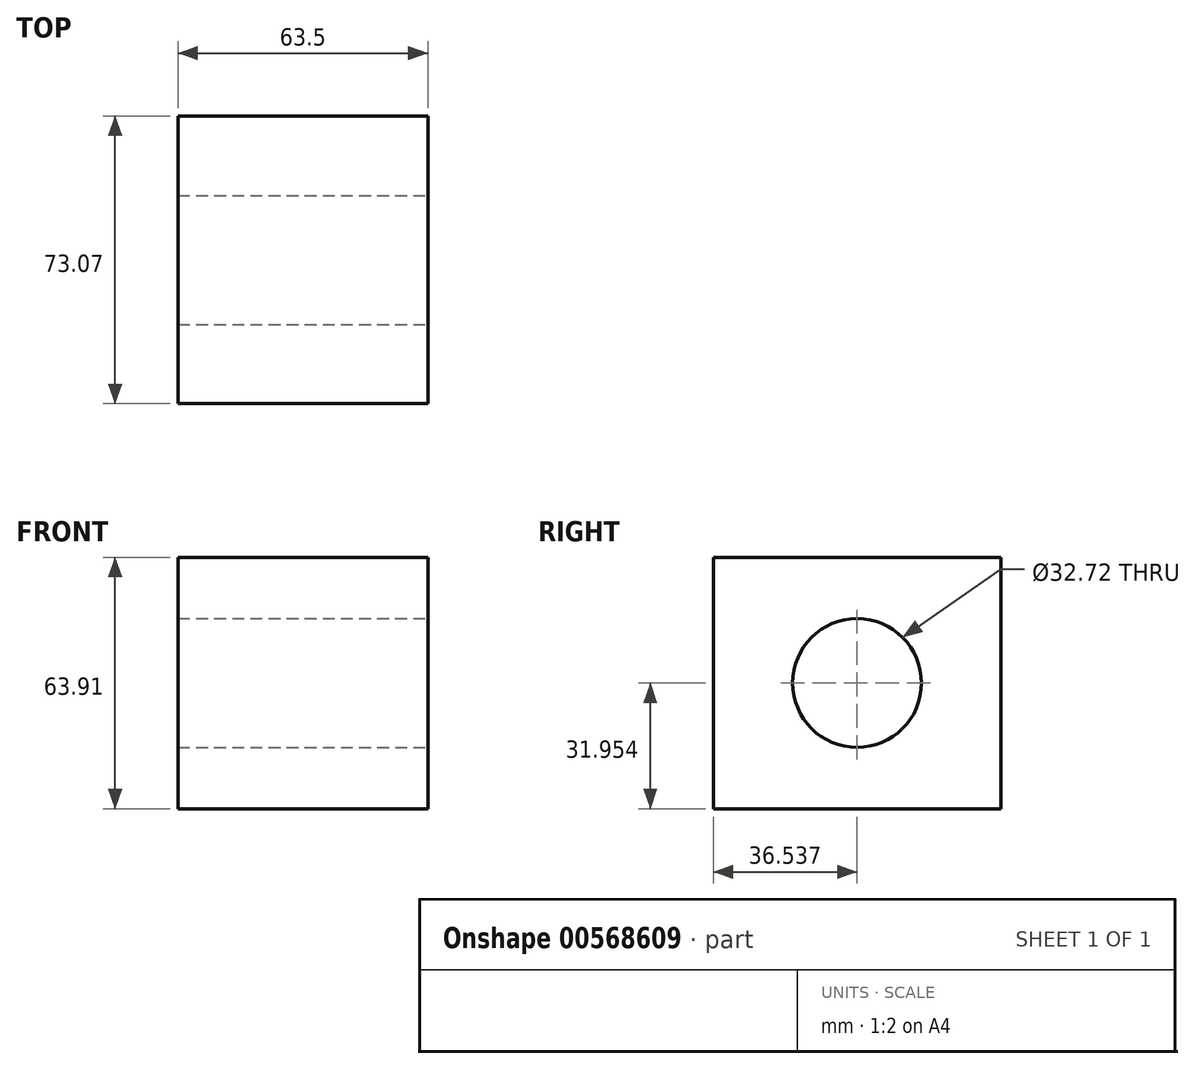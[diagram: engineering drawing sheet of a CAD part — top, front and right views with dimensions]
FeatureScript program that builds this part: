
annotation { "Feature Type Name" : "Feature", "Feature Type Description" : "" }
export const myFeature = defineFeature(function(context is Context, id is Id, definition is map)
    precondition{}
    {
        {
            var Q0;
            Q0=qCreatedBy(makeId("Right.planeOp"),FACE);
            var sketch = newSketch(context, id + "F0", { "sketchPlane" : qUnion([Q0])});
            skLineSegment(sketch, "E0.bottom", {"start": v(0, 0) * mm, "end": v(73.07, 0) * mm});
            skLineSegment(sketch, "E0.top", {"start": v(0, 63.9) * mm, "end": v(73.07, 63.9) * mm});
            skLineSegment(sketch, "E0.left", {"start": v(0, 0) * mm, "end": v(0, 63.9) * mm});
            skLineSegment(sketch, "E0.right", {"start": v(73.07, 0) * mm, "end": v(73.07, 63.9) * mm});
            skSolve(sketch);
        }
        {
            var Q0;
            Q0=makeQuery(id+"F0.imprint","IMPRINT",FACE,{"disambiguationData":[TD([[makeQuery(id+"F0.imprint","IMPRINT",EDGE,{"derivedFrom":sQuery(id+"F0.wireOp",EDGE,"E0.bottom")}),1.0]])]});
            extrude(context, id + "F1", {"entities" : qUnion([Q0]), "depth" : 63.5 * mm, "offsetDistance" : 25.4 * mm});
        }
        {
            var Q0;
            Q0=makeQuery(id+"F1.opExtrude","CAP_FACE",FACE,{"disambiguationData":[OSD([sQuery(id+"F0.wireOp",EDGE,"E0.bottom"),sQuery(id+"F0.wireOp",EDGE,"E0.top"),sQuery(id+"F0.wireOp",EDGE,"E0.left"),sQuery(id+"F0.wireOp",EDGE,"E0.right")])],"isStart":false});
            var sketch = newSketch(context, id + "F2", { "sketchPlane" : qUnion([Q0])});
            skArc(sketch, "E1", {"start": v(33.92, 15.8) * mm, "mid": v(30.07, 19.46) * mm, "end": v(24.87, 20.49) * mm});
            skCircle(sketch, "E2", {"center": v(36.54, 31.95) * mm, "radius": 16.36 * mm});
            skPoint(sketch, "E2.centerSnap0", {"position": v(0, 31.95) * mm});
            skPoint(sketch, "E2.centerSnap1", {"position": v(36.54, 0) * mm});
            skSolve(sketch);
        }
        {
            var Q0;
            Q0 = qSketchRegion(id + "F2", true);
            extrude(context, id + "F3", {"entities" : qUnion([Q0]), "operationType" : NewBodyOperationType.REMOVE, "oppositeDirection" : true, "depth" : 63.5 * mm, "offsetDistance" : 25.4 * mm});
        }
    });
